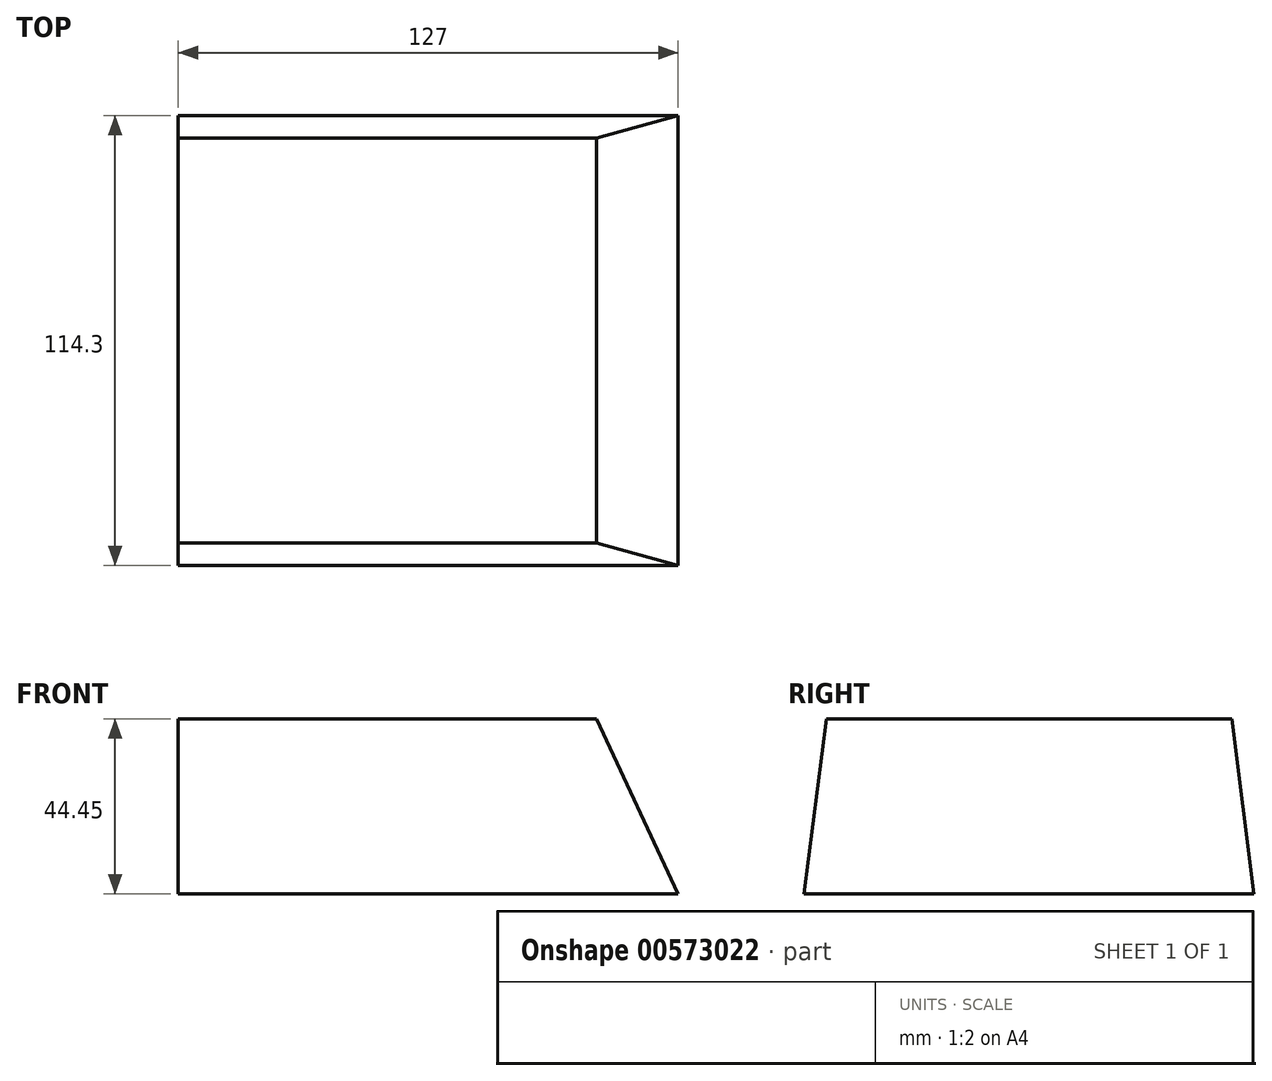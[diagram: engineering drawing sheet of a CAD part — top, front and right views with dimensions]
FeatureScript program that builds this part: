
annotation { "Feature Type Name" : "Feature", "Feature Type Description" : "" }
export const myFeature = defineFeature(function(context is Context, id is Id, definition is map)
    precondition{}
    {
        {
            var Q0;
            Q0=qCreatedBy(makeId("Right.planeOp"),FACE);
            var sketch = newSketch(context, id + "F0", { "sketchPlane" : qUnion([Q0])});
            skLineSegment(sketch, "E0.bottom", {"start": v(-69.73, 15.37) * mm, "end": v(44.57, 15.37) * mm});
            skLineSegment(sketch, "E0.top", {"start": v(-69.73, -29.08) * mm, "end": v(44.57, -29.08) * mm});
            skLineSegment(sketch, "E0.left", {"start": v(-69.73, 15.37) * mm, "end": v(-69.73, -29.08) * mm});
            skLineSegment(sketch, "E0.right", {"start": v(44.57, 15.37) * mm, "end": v(44.57, -29.08) * mm});
            skSolve(sketch);
        }
        {
            var Q0;
            Q0=makeQuery(id+"F0.imprint","IMPRINT",FACE,{"disambiguationData":[TD([[makeQuery(id+"F0.imprint","IMPRINT",EDGE,{"derivedFrom":sQuery(id+"F0.wireOp",EDGE,"E0.bottom")}),-1.0]])]});
            extrude(context, id + "F1", {"entities" : qUnion([Q0]), "depth" : 127 * mm, "offsetDistance" : 25.4 * mm});
        }
        {
            var Q0;
            Q0=qCreatedBy(makeId("Front.planeOp"),FACE);
            var sketch = newSketch(context, id + "F2", { "sketchPlane" : qUnion([Q0])});
            skPoint(sketch, "E1.0", {"position": v(127, -29.08) * mm});
            skLineSegment(sketch, "E2.0", {"start": v(127, 15.37) * mm, "end": v(127, -29.08) * mm});
            skLineSegment(sketch, "E3.0", {"start": v(127, 15.37) * mm, "end": v(0, 15.37) * mm});
            skLineSegment(sketch, "E4", {"start": v(127, -29.08) * mm, "end": v(106.27, 15.37) * mm});
            skLineSegment(sketch, "E5", {"start": v(106.27, 15.37) * mm, "end": v(127, 15.37) * mm});
            skLineSegment(sketch, "E6", {"start": v(127, -29.08) * mm, "end": v(127, 15.37) * mm});
            skSolve(sketch);
        }
        {
            var Q0;
            Q0 = qSketchRegion(id + "F2", true);
            extrude(context, id + "F3", {"entities" : qUnion([Q0]), "operationType" : NewBodyOperationType.REMOVE, "endBound" : BoundingType.SYMMETRIC, "depth" : 254 * mm, "offsetDistance" : 25.4 * mm});
        }
        {
            var Q0;
            Q0=qCreatedBy(makeId("Right.planeOp"),FACE);
            cPlane(context, id + "F4", {"entities" : qUnion([Q0]), "cplaneType" : CPlaneType.OFFSET, "offset" : 25.4 * mm, "width" : 152.4 * mm, "height" : 152.4 * mm});
        }
        {
            var Q0;
            Q0=qCreatedBy(id+"F4.planeOp",FACE);
            var sketch = newSketch(context, id + "F5", { "sketchPlane" : qUnion([Q0])});
            skPoint(sketch, "E7.0", {"position": v(44.57, -29.08) * mm});
            skPoint(sketch, "E8.0", {"position": v(44.57, 15.37) * mm});
            skPoint(sketch, "E9.0", {"position": v(-69.73, -29.08) * mm});
            skPoint(sketch, "E10.0", {"position": v(-12.58, -29.08) * mm});
            skLineSegment(sketch, "E11", {"start": v(44.57, -29.08) * mm, "end": v(10.82, -29.08) * mm});
            skSolve(sketch);
        }
        {
            var Q0;
            Q0=qCreatedBy(id+"F4.planeOp",FACE);
            var sketch = newSketch(context, id + "F6", { "sketchPlane" : qUnion([Q0])});
            skPoint(sketch, "E12.0", {"position": v(44.57, -29.08) * mm});
            skPoint(sketch, "E13.0", {"position": v(44.57, 15.37) * mm});
            skPoint(sketch, "E14.0", {"position": v(-69.73, 15.37) * mm});
            skPoint(sketch, "E15.0", {"position": v(-69.73, -29.08) * mm});
            skPoint(sketch, "E16.0", {"position": v(-12.58, 15.37) * mm});
            skPoint(sketch, "E17.0", {"position": v(-12.58, -29.08) * mm});
            skLineSegment(sketch, "E18", {"start": v(44.57, -29.08) * mm, "end": v(-12.58, -29.08) * mm});
            skLineSegment(sketch, "E19", {"start": v(44.57, -29.08) * mm, "end": v(38.9, 15.37) * mm});
            skLineSegment(sketch, "E20", {"start": v(-12.58, 15.37) * mm, "end": v(-12.58, -29.08) * mm});
            skLineSegment(sketch, "E21.MirrorCS", {"start": v(-69.73, -29.08) * mm, "end": v(-64.07, 15.37) * mm});
            skLineSegment(sketch, "E22.MirrorCS", {"start": v(-69.73, -29.08) * mm, "end": v(-12.58, -29.08) * mm});
            skLineSegment(sketch, "E23", {"start": v(38.9, 15.37) * mm, "end": v(44.57, 15.37) * mm});
            skLineSegment(sketch, "E24", {"start": v(44.57, -29.08) * mm, "end": v(44.57, 15.37) * mm});
            skLineSegment(sketch, "E25", {"start": v(-64.07, 15.37) * mm, "end": v(-69.73, 15.37) * mm});
            skLineSegment(sketch, "E26", {"start": v(-69.73, 15.37) * mm, "end": v(-69.73, -29.08) * mm});
            skSolve(sketch);
        }
        {
            var Q0;
            Q0 = qSketchRegion(id + "F6", true);
            extrude(context, id + "F7", {"entities" : qUnion([Q0]), "operationType" : NewBodyOperationType.REMOVE, "depth" : 139.95 * mm, "offsetDistance" : 25.4 * mm, "hasSecondDirection" : true, "secondDirectionOppositeDirection" : true, "secondDirectionDepth" : 86.61 * mm});
        }
    });
